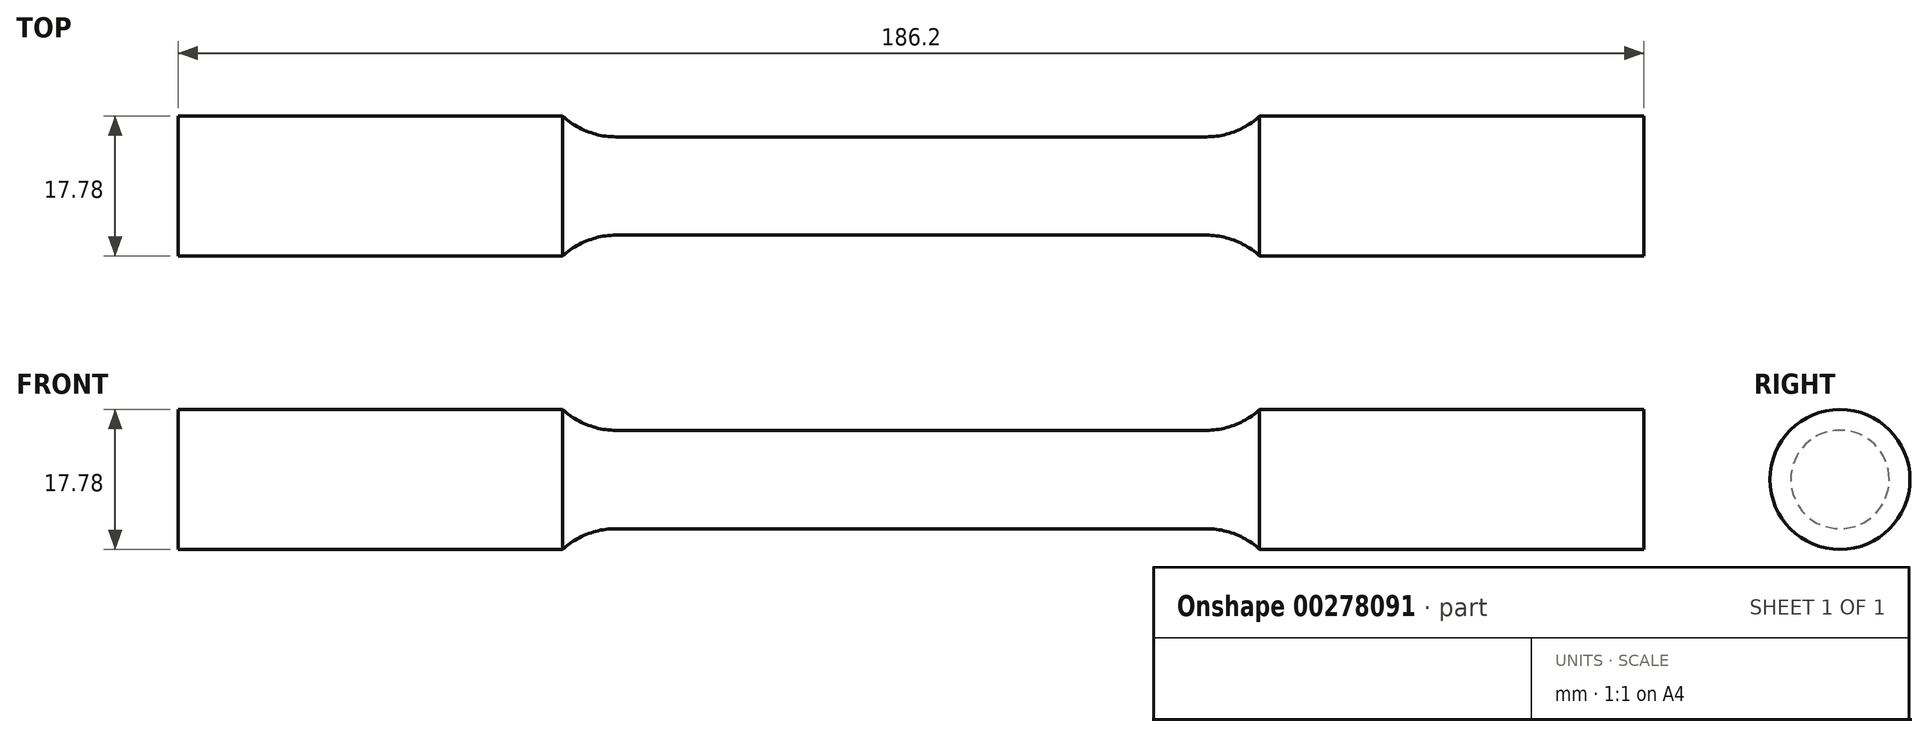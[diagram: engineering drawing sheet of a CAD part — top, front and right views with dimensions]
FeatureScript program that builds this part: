
annotation { "Feature Type Name" : "Feature", "Feature Type Description" : "" }
export const myFeature = defineFeature(function(context is Context, id is Id, definition is map)
    precondition{}
    {
        {
            var Q0;
            Q0=qCreatedBy(makeId("Front.planeOp"),FACE);
            var sketch = newSketch(context, id + "F0", { "sketchPlane" : qUnion([Q0])});
            skLineSegment(sketch, "E0", {"start": v(0, 6.25) * mm, "end": v(37.5, 6.25) * mm});
            skArc(sketch, "E1", {"start": v(37.5, 6.25) * mm, "mid": v(41.14, 6.93) * mm, "end": v(44.27, 8.9) * mm});
            skLineSegment(sketch, "E2", {"start": v(44.27, 8.9) * mm, "end": v(93.1, 8.9) * mm});
            skLineSegment(sketch, "E3", {"start": v(93.1, 8.9) * mm, "end": v(93.1, 0) * mm});
            skLineSegment(sketch, "E4.MirrorCS", {"start": v(-44.27, 8.9) * mm, "end": v(-93.1, 8.9) * mm});
            skArc(sketch, "E5.MirrorCS", {"start": v(-37.5, 6.25) * mm, "mid": v(-41.14, 6.93) * mm, "end": v(-44.27, 8.9) * mm});
            skLineSegment(sketch, "E6.MirrorCS", {"start": v(-93.1, 8.9) * mm, "end": v(-93.1, 0) * mm});
            skLineSegment(sketch, "E7.MirrorCS", {"start": v(0, 6.25) * mm, "end": v(-37.5, 6.25) * mm});
            skLineSegment(sketch, "E8", {"start": v(-93.1, 0) * mm, "end": v(93.1, 0) * mm});
            skSolve(sketch);
        }
        {
            var Q0;
            Q0 = qSketchRegion(id + "F0", true);
            var Q1;
            Q1=sQuery(id+"F0.wireOp",EDGE,"E8");
            revolve(context, id + "F1", {"entities" : qUnion([Q0]), "axis" : qUnion([Q1]), "revolveType" : RevolveType.FULL});
        }
    });
